# Revit family: RBA BIM - 8221
name_source: partatom
category: Specialty Equipment
revit_build: Autodesk Revit 2013 (Build: 20120221_2030)
units: mm (PartAtom-declared; Revit-internal decimal feet)

## types (3) — shared parameters
ADA Compliant = No
Assembly Code = C1030210
Bottle Diameter = 0' - 3 1/4"
Bottle Material = Plastic Bobrick Soap Dispenser White
Bottle Radius = 0' - 1 5/8"
Default Elevation = 4' - 0"
Description = Lavatory-Mounted Soap Dispenser
Fixture Material = Stainless Steel Bobrick
Model = B-Series
Mounting Assembly Material = Plastic Bobrick Soap Dispenser Black
Neck Radius = 0' - 0 1/2"
Top Assembly Height = 0' - 2 1/8"

## per-type parameters (varying)
| type | Assembly Depth | Bottle Depth | Manufacturer | Maximum Mounting Depth | Mounting Depth | Mounting Depth Location | Spout Height | Spout Length | URL |
| B-822 | 1' - 2 5/8" | 0' - 9 9/16" | Bobrick Washroom Equipment, Inc. | 0' - 4" | 0' - 2" | 0' - 2" | 0' - 3" | 0' - 4" | www.bobrick.com |
| B-8221 | 0' - 8 1/4" | 0' - 6 1/8" | Bobrick Washroom Equipment, Inc. | 0' - 1" | 0' - 1" | 0' - 1" | 0' - 3" | 0' - 4" | www.bobrick.com |
| B-8226 | 1' - 2 5/8" | 0' - 9 9/16" | RBA Group | 0' - 4" | 0' - 2" | 0' - 2" | 0' - 3 7/8" | 0' - 6" | www.rba.com.au |

## geometry (parser evidence)
native form markers: Sweep x3
no freeform markers — native parametric forms only
